# Revit family: Kee_Safety_CB1_Radiused_Upright
name_source: partatom
category: Generic Models
units: mm (PartAtom-declared; Revit-internal decimal feet)

## family parameters
Can host rebar = No
Cut with Voids When Loaded = No
Host = Face
Maintain Annotation Orientation = No
Part Type = Normal
Room Calculation Point = No
Round Connector Dimension = Use Diameter
Shared = No

## types (1)
- Kee_Safety_CB1_Radiused_Upright
    Assembly Code = CB1P
    CE Approval = Yes
    Colour = Black/Grey
    Coverage Area = 0 m²
    Default Elevation = 1219 mm
    Description = The recycled PVC weights used with KEEGUARD bring a number of advantages to the system and particularly make
installation quicker and easier thus saving both time and money. Size: 460 x 500 x 85mm, 13.5kg per weight. Carrying
handles moulded into the design. Available in black as standard. Moulded surface to improve grip. Environmentally friendly.
Made from 100% recycled material in the EU.
    Design Country = United Kingdom
    Finish = Galvanised to BS EN ISO 1461/Natural
    Location of Manufacturer = Cradley Heath
    Manufacturer = Kee Safety
    Manufacturer Country = United Kingdom
    Manufacturer Website = www.keesafety.co.uk
    Material = PVC, Unplasticized
    Overall Height = 85 mm  [stored 0.278871 ft]
    Overall Length = 1323 mm
    Overall Width = 500 mm  [stored 1.64042 ft]
    Product Family = KeeGuard
    Product Group = KeeGuard
    Product Model Number = KGA401010
    Product Range = KeeGuard
    Shipping Weight kg = 0.0
    Width = 500 mm  [stored 1.64042 ft]

note: [stored X ft] marks values corroborated as IEEE doubles in the binary element streams (Revit-internal decimal feet)

## geometry (parser evidence)
native form markers: Sweep x10
no freeform markers — native parametric forms only
